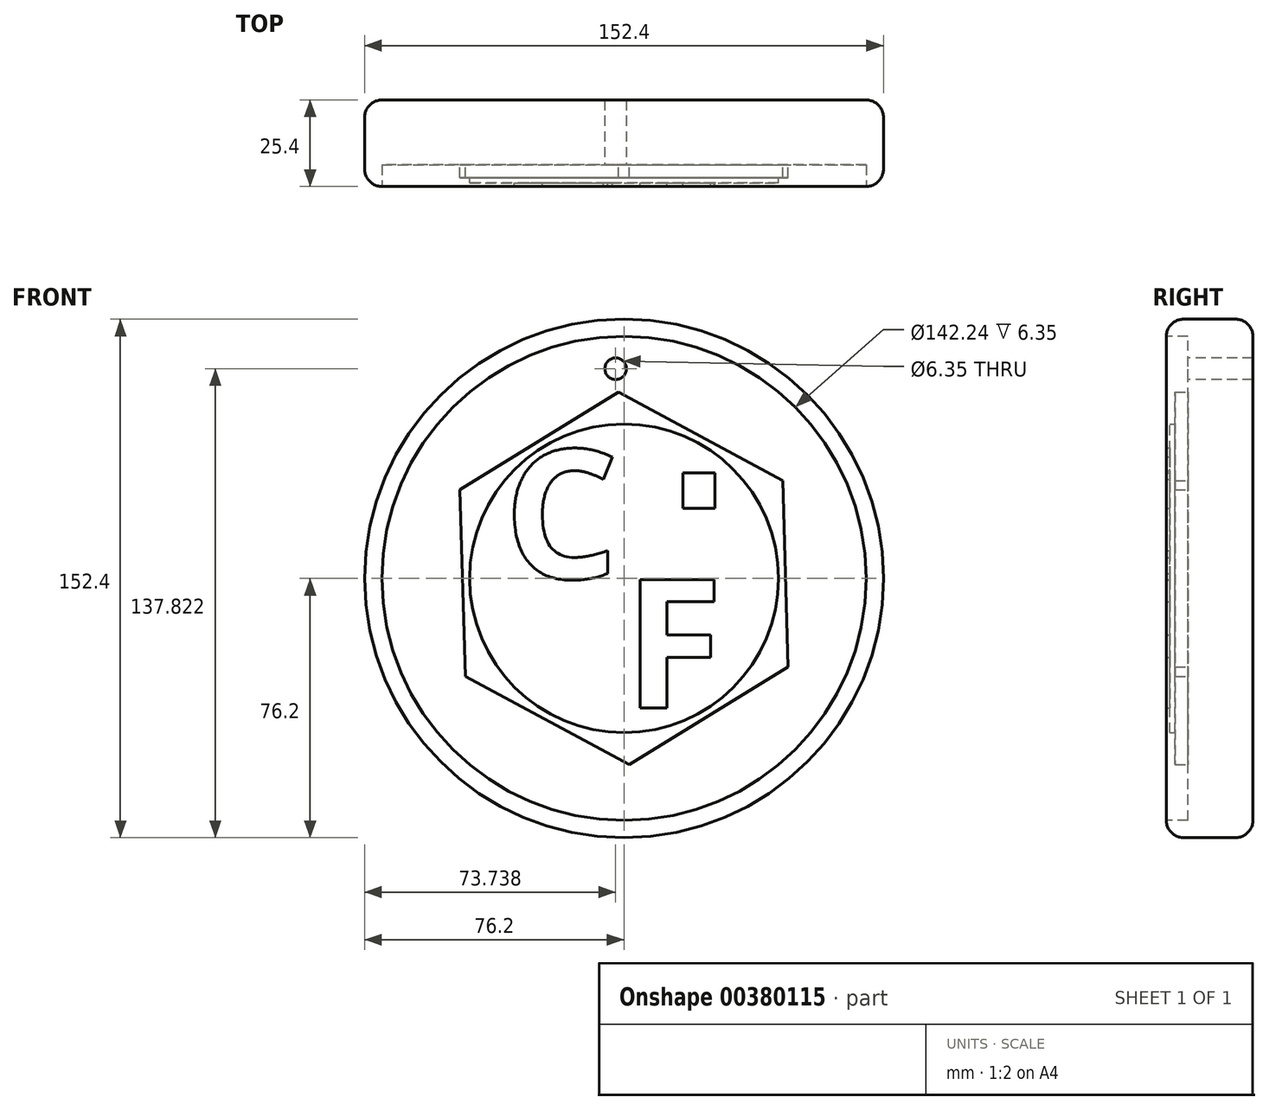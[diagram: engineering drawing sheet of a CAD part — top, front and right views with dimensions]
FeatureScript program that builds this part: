
annotation { "Feature Type Name" : "Feature", "Feature Type Description" : "" }
export const myFeature = defineFeature(function(context is Context, id is Id, definition is map)
    precondition{}
    {
        {
            var Q0;
            Q0=qCreatedBy(makeId("Front.planeOp"),FACE);
            var sketch = newSketch(context, id + "F0", { "sketchPlane" : qUnion([Q0])});
            skCircle(sketch, "E0", {"center": v(0, 0) * mm, "radius": 76.2 * mm});
            skSolve(sketch);
        }
        {
            var Q0;
            Q0 = qSketchRegion(id + "F0", true);
            extrude(context, id + "F1", {"entities" : qUnion([Q0]), "depth" : 25.4 * mm});
        }
        {
            var Q0;
            Q0=makeQuery(id+"F1.opExtrude","CAP_EDGE",EDGE,{"disambiguationData":[OSD([sQuery(id+"F0.wireOp",EDGE,"E0")])],"isStart":false});
            var Q1;
            Q1=makeQuery(id+"F1.opExtrude","CAP_EDGE",EDGE,{"disambiguationData":[OSD([sQuery(id+"F0.wireOp",EDGE,"E0")])],"isStart":true});
            fillet(context, id + "F2", {"entities" : qUnion([Q0, Q1]), "radius" : 5.08 * mm, "tangentPropagation" : true, "allowEdgeOverflow" : false});
        }
        {
            var Q0;
            Q0=makeQuery(id+"F1.opExtrude","CAP_FACE",FACE,{"disambiguationData":[OSD([sQuery(id+"F0.wireOp",EDGE,"E0")])],"isStart":false});
            extrude(context, id + "F3", {"entities" : qUnion([Q0]), "operationType" : NewBodyOperationType.REMOVE, "oppositeDirection" : true, "depth" : 6.35 * mm});
        }
        {
            var Q0;
            Q0=makeQuery(id+"F3.boolean.opBoolean","COPY",FACE,{"derivedFrom":makeQuery(id+"F3.opExtrude","CAP_FACE",FACE,{"disambiguationData":[OSD([sQuery(id+"F0.wireOp",EDGE,"E0")])],"isStart":false})});
            var sketch = newSketch(context, id + "F4", { "sketchPlane" : qUnion([Q0])});
            skText(sketch, "E1", { "text": "C", "fontName": "OpenSans-Bold.ttf"});
            const initialGuessF4  = {"E1": [-0.03529, 0, 1, 0, 0.0381]};
            skSetInitialGuess(sketch, initialGuessF4);
            skSolve(sketch);
        }
        {
            var Q0;
            Q0=makeQuery(id+"F4.imprint","IMPRINT",FACE,{"disambiguationData":[TD([[makeQuery(id+"F4.imprint","IMPRINT",EDGE,{"derivedFrom":sQuery(id+"F4.wireOp",EDGE,"E1.sketch_text.stroke-0")}),1.0]])]});
            var sketch = newSketch(context, id + "F5", { "sketchPlane" : qUnion([Q0])});
            skText(sketch, "E2", { "text": "F", "fontName": "OpenSans-Bold.ttf"});
            const initialGuessF5  = {"E2": [0, -0.0381, 1, 0, 0.0381]};
            skSetInitialGuess(sketch, initialGuessF5);
            skSolve(sketch);
        }
        {
            var Q0;
            Q0 = qSketchRegion(id + "F4", true);
            extrude(context, id + "F6", {"entities" : qUnion([Q0]), "operationType" : NewBodyOperationType.ADD, "depth" : 6.35 * mm});
        }
        {
            var Q0;
            Q0=makeQuery(id+"F5.imprint","IMPRINT",FACE,{"disambiguationData":[TD([[makeQuery(id+"F5.imprint","IMPRINT",EDGE,{"derivedFrom":sQuery(id+"F5.wireOp",EDGE,"E2.sketch_text.stroke-0")}),-1.0]])]});
            extrude(context, id + "F7", {"entities" : qUnion([Q0]), "operationType" : NewBodyOperationType.ADD, "depth" : 6.35 * mm});
        }
        {
            var Q0;
            Q0=makeQuery(id+"F3.boolean.opBoolean","COPY",FACE,{"derivedFrom":makeQuery(id+"F3.opExtrude","CAP_FACE",FACE,{"disambiguationData":[OSD([sQuery(id+"F0.wireOp",EDGE,"E0")])],"isStart":false})});
            var sketch = newSketch(context, id + "F8", { "sketchPlane" : qUnion([Q0])});
            skSolve(sketch);
        }
        {
            var Q0;
            Q0=makeQuery(id+"F8.imprint","IMPRINT",FACE,{"disambiguationData":[TD([[makeQuery(id+"F8.imprint","IMPRINT",EDGE,{"derivedFrom":makeQuery(id+"F3.boolean.opBoolean","COPY",EDGE,{"derivedFrom":makeQuery(id+"F3.opExtrude","CAP_EDGE",EDGE,{"disambiguationData":[OSD([sQuery(id+"F0.wireOp",EDGE,"E0")])],"isStart":false})})}),1.0]])]});
            var sketch = newSketch(context, id + "F9", { "sketchPlane" : qUnion([Q0])});
            skCircle(sketch, "E3", {"center": v(-2.46, 61.62) * mm, "radius": 3.18 * mm});
            skSolve(sketch);
        }
        {
            var Q0;
            Q0 = qSketchRegion(id + "F9", true);
            extrude(context, id + "F10", {"entities" : qUnion([Q0]), "operationType" : NewBodyOperationType.REMOVE, "oppositeDirection" : true, "depth" : 25.4 * mm});
        }
        {
            var Q0;
            Q0=makeQuery(id+"F8.imprint","IMPRINT",FACE,{"disambiguationData":[TD([[makeQuery(id+"F8.imprint","IMPRINT",EDGE,{"derivedFrom":makeQuery(id+"F3.boolean.opBoolean","COPY",EDGE,{"derivedFrom":makeQuery(id+"F3.opExtrude","CAP_EDGE",EDGE,{"disambiguationData":[OSD([sQuery(id+"F0.wireOp",EDGE,"E0")])],"isStart":false})})}),1.0]])]});
            var sketch = newSketch(context, id + "F11", { "sketchPlane" : qUnion([Q0])});
            skCircle(sketch, "E4.cCircle", {"center": v(0, 0) * mm, "radius": 47.44 * mm, "construction": true});
            skLineSegment(sketch, "E4.0", {"start": v(-1.6, 54.75) * mm, "end": v(46.62, 28.75) * mm});
            skLineSegment(sketch, "E4.1", {"start": v(46.62, 28.75) * mm, "end": v(48.21, -26) * mm});
            skLineSegment(sketch, "E4.2", {"start": v(48.21, -26) * mm, "end": v(1.6, -54.75) * mm});
            skLineSegment(sketch, "E4.3", {"start": v(1.6, -54.75) * mm, "end": v(-46.62, -28.75) * mm});
            skLineSegment(sketch, "E4.4", {"start": v(-46.62, -28.75) * mm, "end": v(-48.21, 26) * mm});
            skLineSegment(sketch, "E4.5", {"start": v(-48.21, 26) * mm, "end": v(-1.6, 54.75) * mm});
            skPoint(sketch, "E4.0.midPoint", {"position": v(22.52, 41.75) * mm});
            skSolve(sketch);
        }
        {
            var Q0;
            Q0 = qSketchRegion(id + "F11", true);
            extrude(context, id + "F12", {"entities" : qUnion([Q0]), "operationType" : NewBodyOperationType.ADD, "depth" : 3.8 * mm});
        }
        {
            var Q0;
            Q0=makeQuery(id+"F12.opExtrude","CAP_FACE",FACE,{"disambiguationData":[OSD([sQuery(id+"F11.wireOp",EDGE,"E4.0"),sQuery(id+"F11.wireOp",EDGE,"E4.1"),sQuery(id+"F11.wireOp",EDGE,"E4.2"),sQuery(id+"F11.wireOp",EDGE,"E4.3"),sQuery(id+"F11.wireOp",EDGE,"E4.4"),sQuery(id+"F11.wireOp",EDGE,"E4.5")])],"isStart":false});
            var sketch = newSketch(context, id + "F13", { "sketchPlane" : qUnion([Q0])});
            skSolve(sketch);
        }
        {
            var Q0;
            {var subQ5=sQuery(id+"F11.wireOp",EDGE,"E4.0");Q0=makeQuery(id+"F13.imprint","IMPRINT",FACE,{"disambiguationData":[TD([[makeQuery(id+"F13.imprint","IMPRINT",EDGE,{"derivedFrom":makeQuery(id+"F12.opExtrude","CAP_EDGE",EDGE,{"disambiguationData":[OSD([subQ5])],"isStart":false})}),-1.0]])]});}
            var sketch = newSketch(context, id + "F14", { "sketchPlane" : qUnion([Q0])});
            skLineSegment(sketch, "E5.bottom", {"start": v(17.35, 20.55) * mm, "end": v(26.66, 20.55) * mm});
            skLineSegment(sketch, "E5.top", {"start": v(17.35, 30.96) * mm, "end": v(26.66, 30.96) * mm});
            skLineSegment(sketch, "E5.left", {"start": v(17.35, 20.55) * mm, "end": v(17.35, 30.96) * mm});
            skLineSegment(sketch, "E5.right", {"start": v(26.66, 20.55) * mm, "end": v(26.66, 30.96) * mm});
            skSolve(sketch);
        }
        {
            var Q0;
            Q0 = qSketchRegion(id + "F14", true);
            extrude(context, id + "F15", {"entities" : qUnion([Q0]), "operationType" : NewBodyOperationType.ADD, "depth" : 2.54 * mm});
        }
        {
            var Q0;
            {var subQ5=sQuery(id+"F11.wireOp",EDGE,"E4.0");Q0=makeQuery(id+"F13.imprint","IMPRINT",FACE,{"disambiguationData":[TD([[makeQuery(id+"F13.imprint","IMPRINT",EDGE,{"derivedFrom":makeQuery(id+"F12.opExtrude","CAP_EDGE",EDGE,{"disambiguationData":[OSD([subQ5])],"isStart":false})}),-1.0]])]});}
            var sketch = newSketch(context, id + "F16", { "sketchPlane" : qUnion([Q0])});
            skCircle(sketch, "E6", {"center": v(-23.6, -15.52) * mm, "radius": 8.45 * mm});
            skSolve(sketch);
        }
        {
            var Q0;
            Q0=sQuery(id+"F16.wireOp",EDGE,"E6");
            extrude(context, id + "F17", {"bodyType" : ToolBodyType.SURFACE, "surfaceEntities" : qUnion([Q0]), "depth" : 2.54 * mm});
        }
        {
            var Q0;
            {var subQ5=sQuery(id+"F11.wireOp",EDGE,"E4.0");Q0=makeQuery(id+"F13.imprint","IMPRINT",FACE,{"disambiguationData":[TD([[makeQuery(id+"F13.imprint","IMPRINT",EDGE,{"derivedFrom":makeQuery(id+"F12.opExtrude","CAP_EDGE",EDGE,{"disambiguationData":[OSD([subQ5])],"isStart":false})}),-1.0]])]});}
            var sketch = newSketch(context, id + "F18", { "sketchPlane" : qUnion([Q0])});
            skSolve(sketch);
        }
        {
            var Q0;
            {var subQ5=sQuery(id+"F11.wireOp",EDGE,"E4.0");Q0=makeQuery(id+"F18.imprint","IMPRINT",FACE,{"disambiguationData":[TD([[makeQuery(id+"F18.imprint","IMPRINT",EDGE,{"derivedFrom":makeQuery(id+"F13.imprint","IMPRINT",EDGE,{"derivedFrom":makeQuery(id+"F12.opExtrude","CAP_EDGE",EDGE,{"disambiguationData":[OSD([subQ5])],"isStart":false})})}),-1.0]])]});}
            var sketch = newSketch(context, id + "F19", { "sketchPlane" : qUnion([Q0])});
            skCircle(sketch, "E7", {"center": v(0, 0) * mm, "radius": 45.36 * mm});
            skSolve(sketch);
        }
        {
            var Q0;
            Q0 = qSketchRegion(id + "F19", true);
            extrude(context, id + "F20", {"entities" : qUnion([Q0]), "operationType" : NewBodyOperationType.ADD, "depth" : 1.52 * mm});
        }
    });
